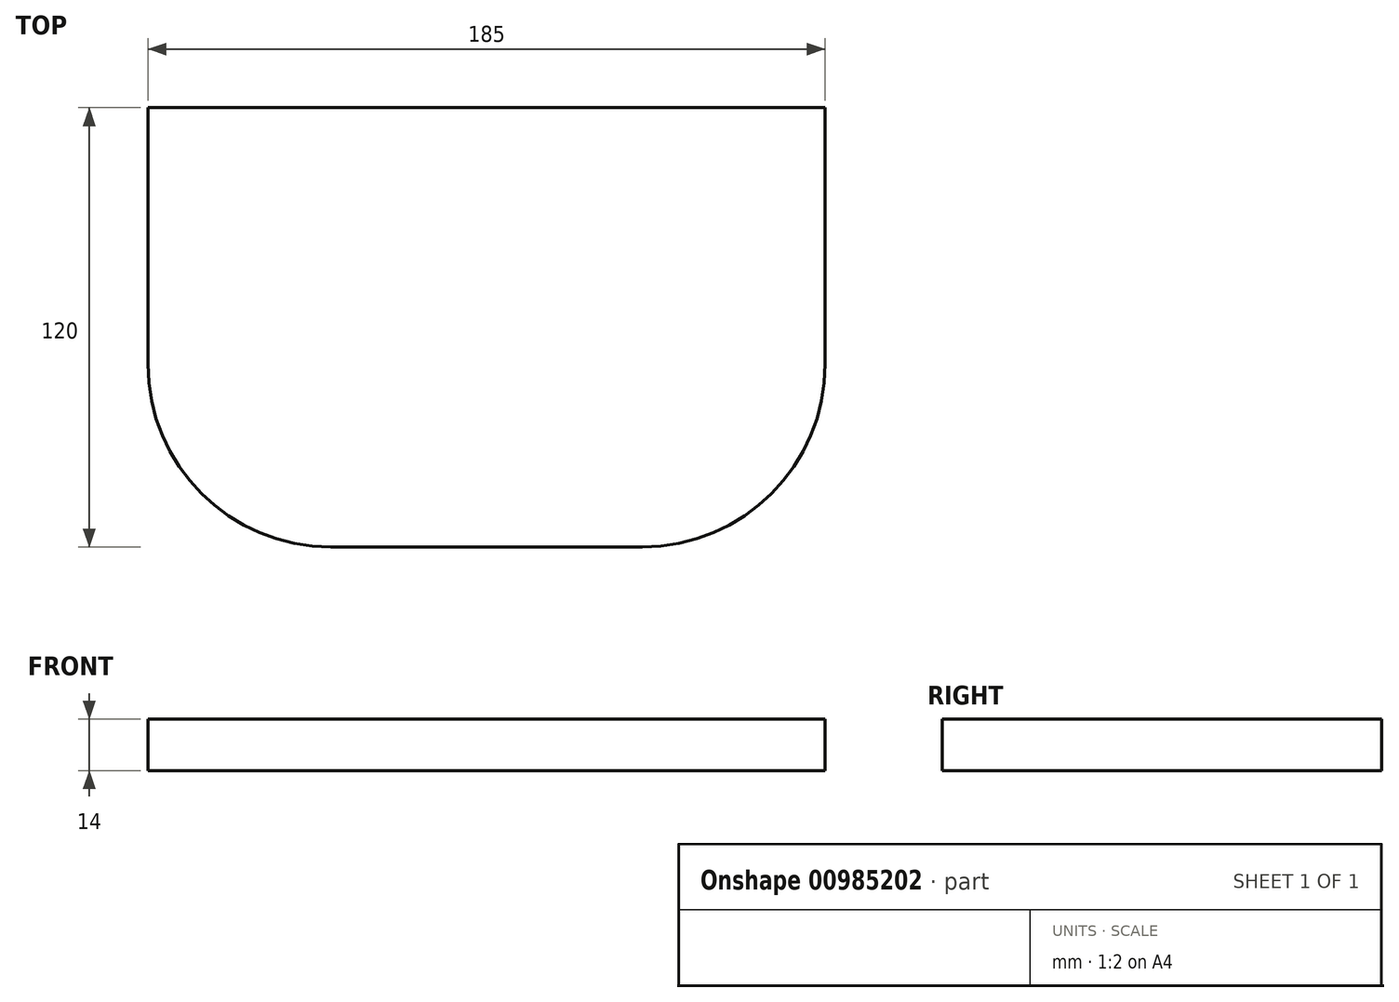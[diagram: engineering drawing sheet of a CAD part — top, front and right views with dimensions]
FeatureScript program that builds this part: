
annotation { "Feature Type Name" : "Feature", "Feature Type Description" : "" }
export const myFeature = defineFeature(function(context is Context, id is Id, definition is map)
    precondition{}
    {
        {
            var Q0;
            Q0=qCreatedBy(makeId("Top.planeOp"),FACE);
            var sketch = newSketch(context, id + "F0", { "sketchPlane" : qUnion([Q0])});
            skLineSegment(sketch, "E0.bottom", {"start": v(-92.5, 0) * mm, "end": v(92.5, 0) * mm});
            skLineSegment(sketch, "E0.top", {"start": v(-42.5, -120) * mm, "end": v(42.5, -120) * mm});
            skLineSegment(sketch, "E0.left", {"start": v(-92.5, 0) * mm, "end": v(-92.5, -70) * mm});
            skLineSegment(sketch, "E0.right", {"start": v(92.5, 0) * mm, "end": v(92.5, -70) * mm});
            skPoint(sketch, "E1.visualSharp", {"position": v(-92.5, -120) * mm});
            skArc(sketch, "E1.filletArc", {"start": v(-92.5, -70) * mm, "mid": v(-77.86, -105.36) * mm, "end": v(-42.5, -120) * mm});
            skPoint(sketch, "E2.visualSharp", {"position": v(92.5, -120) * mm});
            skArc(sketch, "E2.filletArc", {"start": v(42.5, -120) * mm, "mid": v(77.86, -105.36) * mm, "end": v(92.5, -70) * mm});
            skSolve(sketch);
        }
        {
            var Q0;
            Q0 = qSketchRegion(id + "F0", true);
            extrude(context, id + "F1", {"entities" : qUnion([Q0]), "depth" : 14 * mm, "offsetDistance" : 25 * mm});
        }
    });
